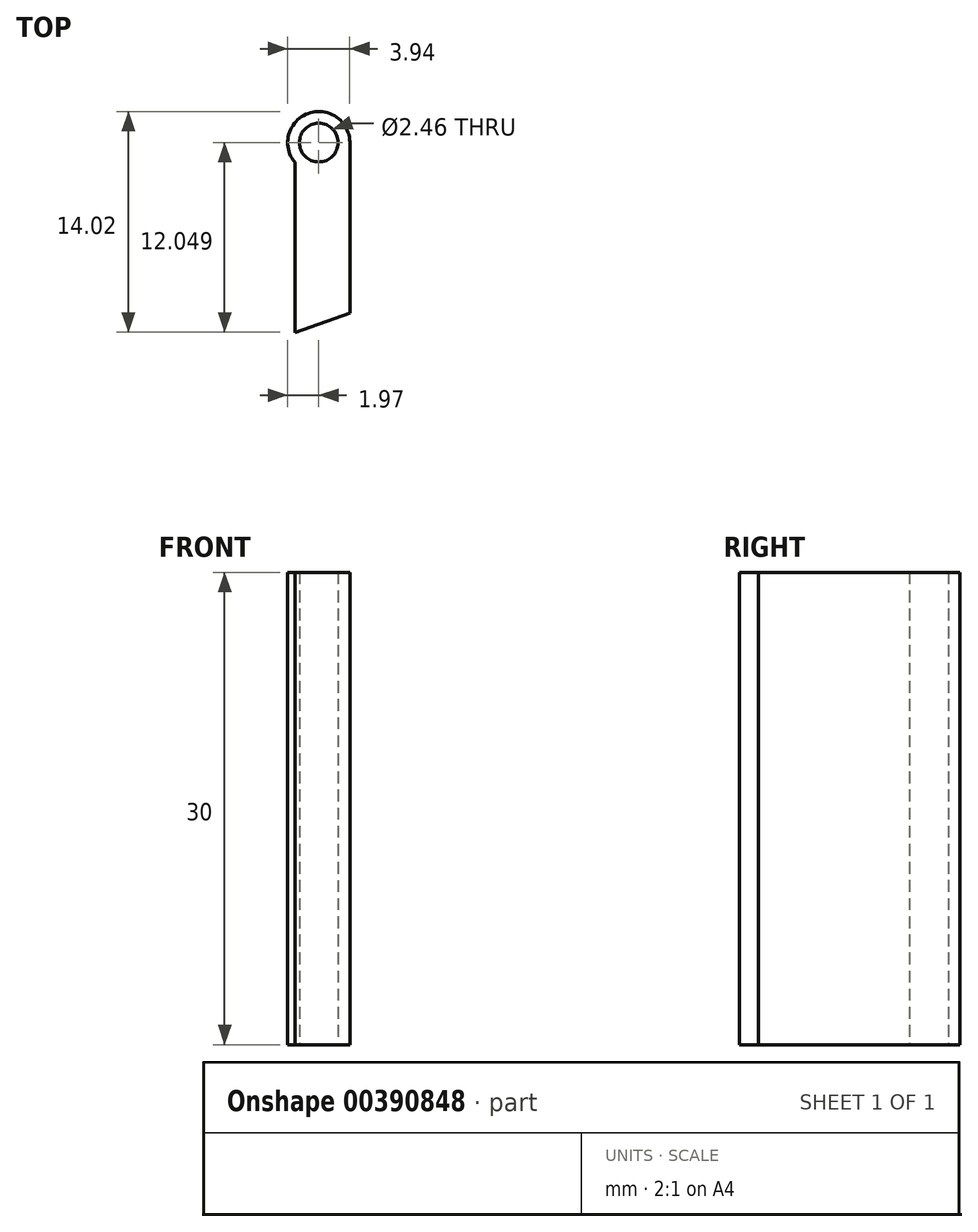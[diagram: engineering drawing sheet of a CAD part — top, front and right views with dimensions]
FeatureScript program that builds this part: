
annotation { "Feature Type Name" : "Feature", "Feature Type Description" : "" }
export const myFeature = defineFeature(function(context is Context, id is Id, definition is map)
    precondition{}
    {
        {
            var Q0;
            Q0=qCreatedBy(makeId("Top.planeOp"),FACE);
            var sketch = newSketch(context, id + "F0", { "sketchPlane" : qUnion([Q0])});
            skLineSegment(sketch, "E0.left", {"start": v(-1.52, -5.34) * mm, "end": v(-1.52, 5.48) * mm});
            skLineSegment(sketch, "E0.right", {"start": v(1.52, 5.46) * mm, "end": v(1.52, 5.48) * mm});
            skPoint(sketch, "E0.middle", {"position": v(0, 0.07) * mm});
            skCircle(sketch, "E1", {"center": v(0, 6.7) * mm, "radius": 1.23 * mm});
            skArc(sketch, "E2", {"start": v(1.97, 6.7) * mm, "mid": v(-0.66, 8.57) * mm, "end": v(-1.52, 5.46) * mm});
            skLineSegment(sketch, "E3", {"start": v(-1.52, -5.34) * mm, "end": v(1.97, -4.13) * mm});
            skLineSegment(sketch, "E4", {"start": v(1.97, -4.13) * mm, "end": v(1.97, 6.73) * mm});
            skSolve(sketch);
        }
        {
            var Q0;
            Q0=makeQuery(id+"F0.imprint","IMPRINT",FACE,{"disambiguationData":[TD([[makeQuery(id+"F0.imprint","IMPRINT",EDGE,{"derivedFrom":sQuery(id+"F0.wireOp",EDGE,"E1")}),-1.0]])]});
            extrude(context, id + "F1", {"entities" : qUnion([Q0]), "depth" : 30 * mm});
        }
    });
